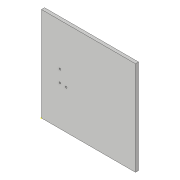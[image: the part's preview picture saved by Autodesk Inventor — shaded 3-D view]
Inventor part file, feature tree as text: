
AUTODESK INVENTOR PART (.ipt)
format: ipt  version: 2019 (Build 230136000, 136)  size: 91,136 bytes
history: native  units: in
note: dims shown in document units (in); Inventor stores cm internally (conversion verified against a paired STEP export)
features: sketch x7, extrude x3
ambient origin geometry x8: Origin, YZ Plane, XZ Plane, XY Plane, X Axis, Y Axis, Z Axis, Center Point
bodies: Solid1 (feature_tree)
feature tree (10):
  extrude  "Extrusion1"  Depth=24.0in
  sketch  "Sketch2"  dims[d2=0.7874in d3=0.0in d4=0.4331in]
  sketch  "Sketch3"  dims[d5=0.0in d6=0.0in d7=4.7244in]
  sketch  "Sketch4"  dims[d8=0.4331in]
  extrude  "Extrusion2"  Depth=0.7874in
  sketch  "Sketch6"  dims[d10=0.0in d11=0.0in]
  extrude  "Extrusion3"  Depth=4.7244in
  sketch  "Sketch1"  dims[d0=24.0in d1=24.0in]
  sketch  "Sketch5"  dims[d9=0.4331in]
  sketch  "Sketch7"
